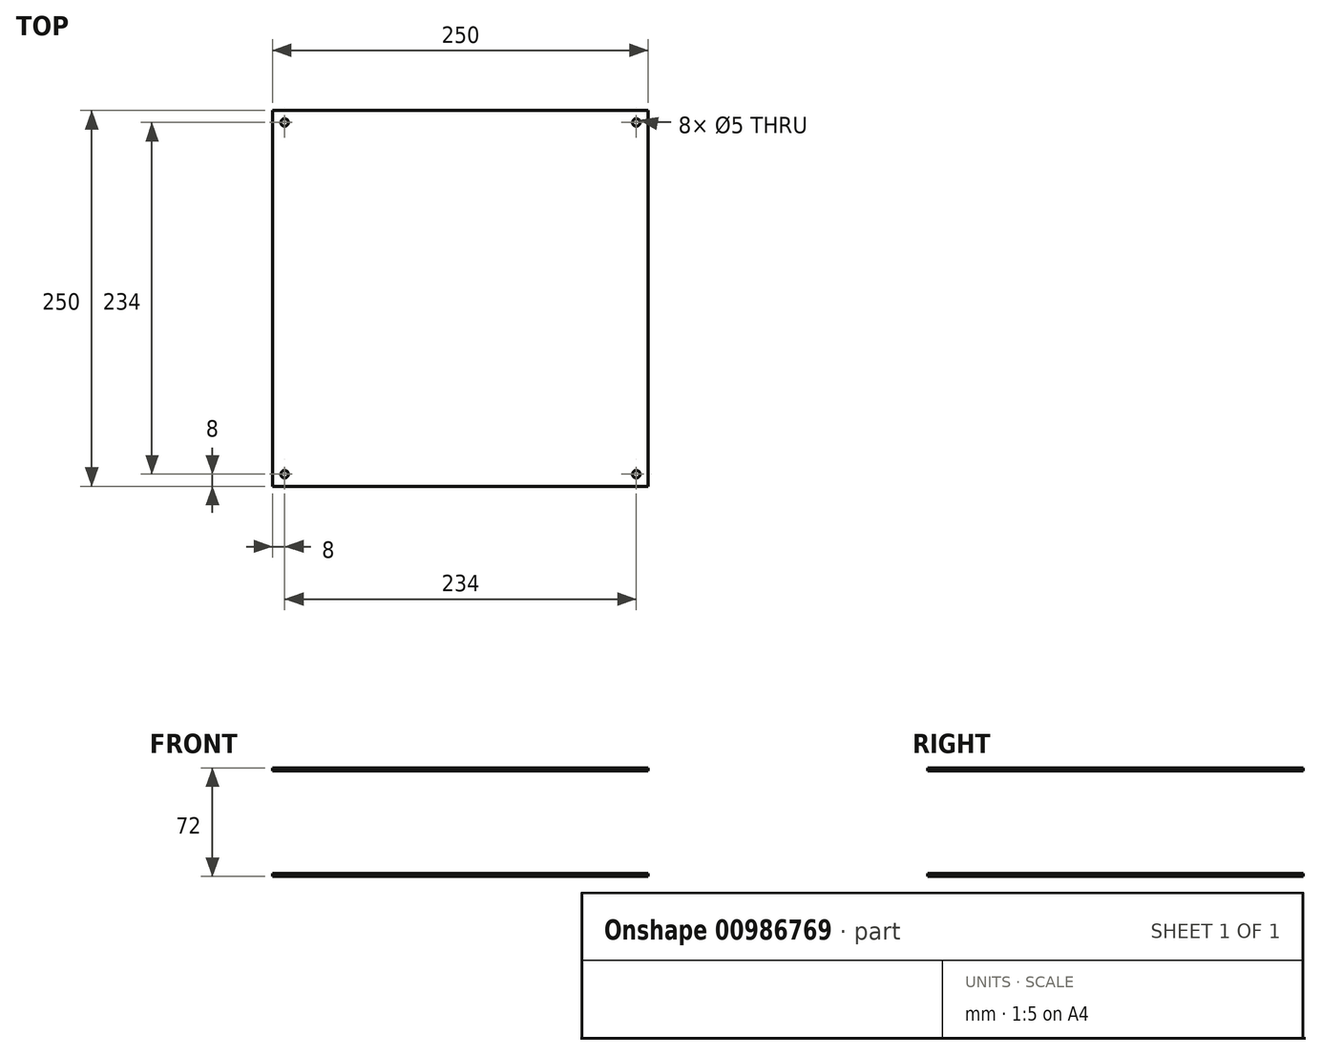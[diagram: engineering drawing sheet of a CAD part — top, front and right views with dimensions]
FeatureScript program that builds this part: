
annotation { "Feature Type Name" : "Feature", "Feature Type Description" : "" }
export const myFeature = defineFeature(function(context is Context, id is Id, definition is map)
    precondition{}
    {
        {
            var Q0;
            Q0=qCreatedBy(makeId("Top.planeOp"),FACE);
            var sketch = newSketch(context, id + "F0", { "sketchPlane" : qUnion([Q0])});
            skLineSegment(sketch, "E0.bottom", {"start": v(-125, 125) * mm, "end": v(125, 125) * mm});
            skLineSegment(sketch, "E0.top", {"start": v(-125, -125) * mm, "end": v(125, -125) * mm});
            skLineSegment(sketch, "E0.left", {"start": v(-125, 125) * mm, "end": v(-125, -125) * mm});
            skLineSegment(sketch, "E0.right", {"start": v(125, 125) * mm, "end": v(125, -125) * mm});
            skCircle(sketch, "E1", {"center": v(-117, -117) * mm, "radius": 2.5 * mm});
            skCircle(sketch, "E2", {"center": v(117, -117) * mm, "radius": 2.5 * mm});
            skCircle(sketch, "E3", {"center": v(117, 117) * mm, "radius": 2.5 * mm});
            skCircle(sketch, "E4", {"center": v(-117, 117) * mm, "radius": 2.5 * mm});
            skSolve(sketch);
        }
        {
            var Q0;
            Q0=makeQuery(id+"F0.imprint","IMPRINT",FACE,{"disambiguationData":[TD([[makeQuery(id+"F0.imprint","IMPRINT",EDGE,{"derivedFrom":sQuery(id+"F0.wireOp",EDGE,"E0.bottom")}),-1.0]])]});
            extrude(context, id + "F1", {"entities" : qUnion([Q0]), "depth" : 2 * mm, "offsetDistance" : 25 * mm});
        }
        {
            var Q0;
            Q0=makeQuery(id+"F1.opExtrude","SWEPT_BODY",BODY,{"disambiguationData":[OSD([sQuery(id+"F0.wireOp",EDGE,"E0.bottom"),sQuery(id+"F0.wireOp",EDGE,"E0.top"),sQuery(id+"F0.wireOp",EDGE,"E0.left"),sQuery(id+"F0.wireOp",EDGE,"E0.right")])]});
            transform(context, id + "F2", {"entities" : qUnion([Q0]), "transformType" : TransformType.TRANSLATION_3D, "dx" : 0 * mm, "dy" : 0 * mm, "dz" : 70 * mm, "makeCopy" : true});
        }
    });
